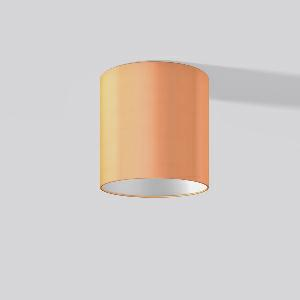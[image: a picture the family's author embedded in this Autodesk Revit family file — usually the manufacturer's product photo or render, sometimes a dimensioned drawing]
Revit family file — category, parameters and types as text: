
# Revit family: toledo_flatliner_901630_002_112d
name_source: partatom
category: Lighting Fixtures
units: mm (PartAtom-declared; Revit-internal decimal feet)

## family parameters
Cut with Voids When Loaded = No
Host = Face
Light Source = No
Part Type = Normal
Room Calculation Point = No
Round Connector Dimension = Use Diameter
Shared = No

## types (1)
- 982300.002 (1 x LED Modul 830, 610 lm, 3000)
    Apparent Load = 8 VA
    CIE Flux Codes = 56 78 92 81 100
    Color Rendering = 80
    Color Temperature = 3000
    Default Elevation = 1800 mm
    Description = Series: TOLEDO FLATLINER
Decorative ceiling luminaire for interior decoration. Base luminaire prepared for the installation of fabric lampshade. Cylinder housing sheet steel, powder-coated. Housing: die cast aluminium and sheet steel, powder-coated. Bezel ring: die-cast aluminium, powder-coated. Lightguide and diffuser made of non-yellowing plastic (PMMA) opal matt. Modular design: With the basic luminaire, a square or cylindrical fabric lampshade must always be ordered separately. Fabric lampshades can be fitted to the basic luminaire without tools. Order satin finish diffuser as separate accessory. 
Colour: white
Diameter: 202 mm
Height: 65 mm
Lamp: LED
Socket: without socket
Colour temperature: 3000K
Colour rendering index (CRI): 80
System power: 7.7 W
Rated luminous flux: 610 lm
Luminous efficiency: 79 lm/W
Control gear: Regulated power supply
Protection class: II
Type of protection: IP 40
    Height = 65 mm
    Lamp = 1 x LED Modul 830
    Lamp Light Flux = 610 lm
    Lamp count = 1
    Length = 202 mm
    Lifetime = 50000 h
    Luminous efficacy = 79 lm/W
    Manufacturer = RZB
    ModVariant = No
    Model = 901630.002
    Mounting Place = Ceiling
    Mounting Type = Surface mounted
    Number of Poles = 1
    OnlyDefault = Yes
    Power Factor = 1
    Product Name = TOLEDO FLATLINER
    Product group = Surface mounted ceiling Fabric lampshade luminaires
    ProductGroupID = 313
    Protection Class = Protection class II
    Protection Degree = IP 40
    RLX_Detail_Level = 1
    RLX_Emergency_Light_Flux = 0 lm
    RLX_Emergency_Type = 0
    RLX_Emergency_Type_DB = No
    RlxData = <blob elided: 62693 chars, md5=effcb2b1>
    Socket = socket
    Standby Power = 0 W
    System Light Flux = 610 lm
    System Power = 8 W
    Type Image = toledo_flatliner_anbau_rund_orange_odeckel.jpg
    URL = http://relux.com
    VarID = 982300_002_5a54
    Voltage = 230 V
    Voltage Range = 220-240 V
    Weight = 0.00 kg
    Width = 0 mm  [stored 0 ft]

note: [stored X ft] marks values corroborated as IEEE doubles in the binary element streams (Revit-internal decimal feet)

## geometry (parser evidence)
native form markers: Blend x4, Sweep x12
no freeform markers — native parametric forms only
